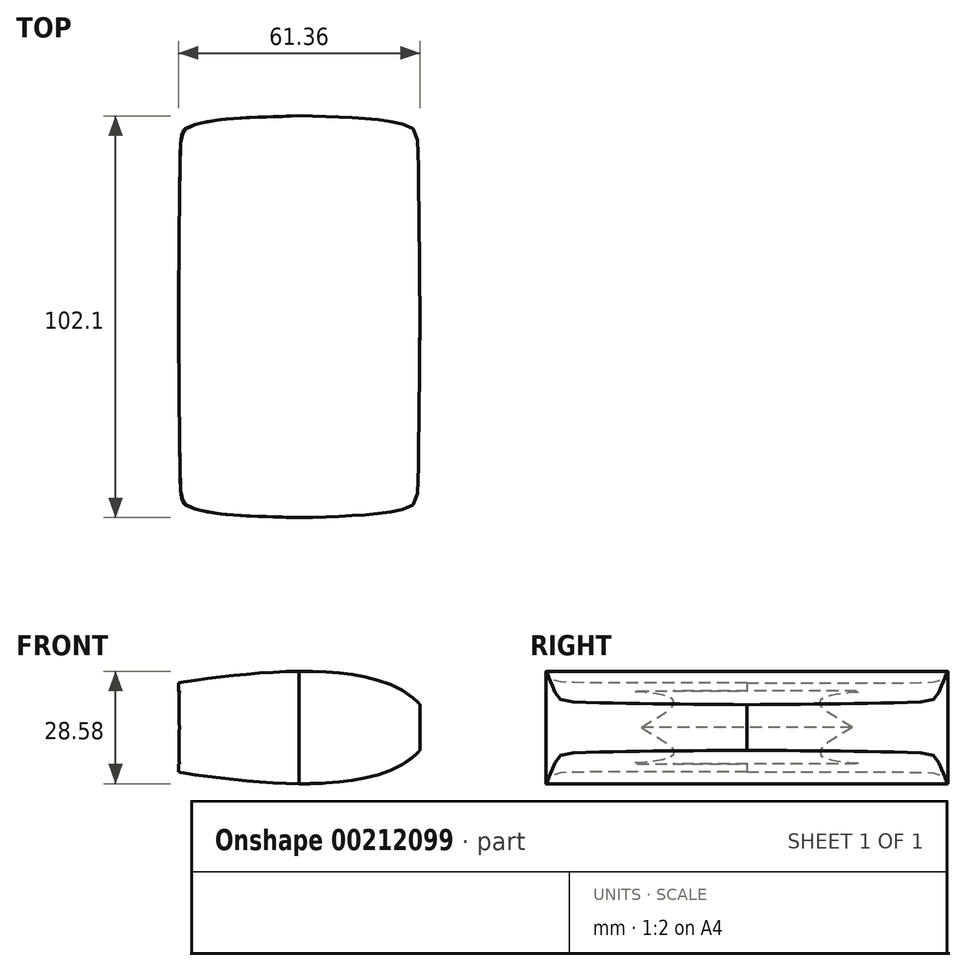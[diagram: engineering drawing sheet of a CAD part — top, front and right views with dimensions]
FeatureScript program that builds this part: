
annotation { "Feature Type Name" : "Feature", "Feature Type Description" : "" }
export const myFeature = defineFeature(function(context is Context, id is Id, definition is map)
    precondition{}
    {
        {
            var Q0;
            Q0=qCreatedBy(makeId("Top.planeOp"),FACE);
            var sketch = newSketch(context, id + "F0", { "sketchPlane" : qUnion([Q0])});
            skLineSegment(sketch, "E0", {"start": v(-32.01, -51) * mm, "end": v(32.01, 51) * mm, "construction": true});
            skSolve(sketch);
        }
        {
            var Q0;
            Q0=qCreatedBy(makeId("Top.planeOp"),FACE);
            var sketch = newSketch(context, id + "F1", { "sketchPlane" : qUnion([Q0])});
            skFitSpline(sketch, "E1", {"points": [v(0, 51.05) * mm, v(12.4, 50.6) * mm, v(22.7, 49.68) * mm, v(28.76, 47.96) * mm, v(29.69, 46.84) * mm, v(30.08, 43.93) * mm, v(30.68, 0) * mm], "startDerivative": vector(67.42, -2.1) * mm, "endDerivative": vector(1.23, -160.86) * mm});
            skFitSpline(sketch, "E2.MirrorCS", {"points": [v(0, 51.05) * mm, v(-12.4, 50.6) * mm, v(-22.7, 49.68) * mm, v(-28.76, 47.96) * mm, v(-29.69, 46.84) * mm, v(-30.08, 43.93) * mm, v(-30.68, 0) * mm], "startDerivative": vector(-67.42, -2.1) * mm, "endDerivative": vector(-1.23, -160.86) * mm});
            skFitSpline(sketch, "E3.MirrorCS", {"points": [v(0, -51.05) * mm, v(12.4, -50.6) * mm, v(22.7, -49.68) * mm, v(28.76, -47.96) * mm, v(29.69, -46.84) * mm, v(30.08, -43.93) * mm, v(30.68, 0) * mm], "startDerivative": vector(67.42, 2.1) * mm, "endDerivative": vector(1.23, 160.86) * mm});
            skFitSpline(sketch, "E4.MirrorCS", {"points": [v(0, -51.05) * mm, v(-12.4, -50.6) * mm, v(-22.7, -49.68) * mm, v(-28.76, -47.96) * mm, v(-29.69, -46.84) * mm, v(-30.08, -43.93) * mm, v(-30.68, 0) * mm], "startDerivative": vector(-67.42, 2.1) * mm, "endDerivative": vector(-1.23, 160.86) * mm});
            skSolve(sketch);
        }
        {
            var Q0;
            Q0=qCreatedBy(makeId("Front.planeOp"),FACE);
            var sketch = newSketch(context, id + "F2", { "sketchPlane" : qUnion([Q0])});
            skLineSegment(sketch, "E5", {"start": v(-34, -17.73) * mm, "end": v(34, 17.73) * mm, "construction": true});
            skLineSegment(sketch, "E6", {"start": v(30.77, 1.5) * mm, "end": v(30.77, -0.25) * mm});
            skPoint(sketch, "E7", {"position": v(30.77, 0.63) * mm});
            skLineSegment(sketch, "E8", {"start": v(30.77, 0.63) * mm, "end": v(-30.44, 0.63) * mm, "construction": true});
            skFitSpline(sketch, "E9", {"points": [v(-30.44, 0.63) * mm, v(-30.44, 9.58) * mm, v(-30.44, 9.85) * mm, v(-31.2, 9.83) * mm, v(-31.86, 10.3) * mm, v(-31.86, 11.26) * mm, v(-30.92, 11.83) * mm, v(-2.82, 14.84) * mm, v(18.3, 13.12) * mm, v(26.86, 9.62) * mm, v(31.88, 4.36) * mm, v(31.88, 1.46) * mm, v(31.3, 1.5) * mm, v(30.77, 1.5) * mm], "startDerivative": vector(-2, 104.73) * mm, "endDerivative": vector(-18.25, -1.93) * mm});
            skFitSpline(sketch, "E10.MirrorCS", {"points": [v(-30.44, 0.63) * mm, v(-30.44, -8.32) * mm, v(-30.44, -8.6) * mm, v(-31.2, -8.57) * mm, v(-31.86, -9.04) * mm, v(-31.86, -10) * mm, v(-30.92, -10.57) * mm, v(-2.82, -13.59) * mm, v(18.3, -11.86) * mm, v(26.86, -8.37) * mm, v(31.88, -3.1) * mm, v(31.88, -0.2) * mm, v(31.3, -0.24) * mm, v(30.77, -0.25) * mm], "startDerivative": vector(-2, -104.73) * mm, "endDerivative": vector(-18.25, 1.93) * mm});
            skLineSegment(sketch, "E11.bottom", {"start": v(-55.61, 30.39) * mm, "end": v(55.61, 30.39) * mm});
            skLineSegment(sketch, "E11.top", {"start": v(-55.61, -30.39) * mm, "end": v(55.61, -30.39) * mm});
            skLineSegment(sketch, "E11.left", {"start": v(-55.61, 30.39) * mm, "end": v(-55.61, -30.39) * mm});
            skLineSegment(sketch, "E11.right", {"start": v(55.61, 30.39) * mm, "end": v(55.61, -30.39) * mm});
            skPoint(sketch, "E11.middle", {"position": v(0, 0) * mm});
            skSolve(sketch);
        }
        {
            var Q0;
            Q0 = qSketchRegion(id + "F1", true);
            extrude(context, id + "F3", {"entities" : qUnion([Q0]), "depth" : 25 * mm, "hasSecondDirection" : true, "secondDirectionOppositeDirection" : true, "secondDirectionDepth" : 25 * mm});
        }
        {
            var Q0;
            Q0=makeQuery(id+"F2.imprint","IMPRINT",FACE,{"disambiguationData":[TD([[makeQuery(id+"F2.imprint","IMPRINT",EDGE,{"derivedFrom":sQuery(id+"F2.wireOp",EDGE,"E6")}),1.0]])]});
            extrude(context, id + "F4", {"entities" : qUnion([Q0]), "operationType" : NewBodyOperationType.REMOVE, "oppositeDirection" : true, "depth" : 150 * mm, "hasSecondDirection" : true, "secondDirectionOppositeDirection" : false, "secondDirectionDepth" : 150 * mm});
        }
    });
